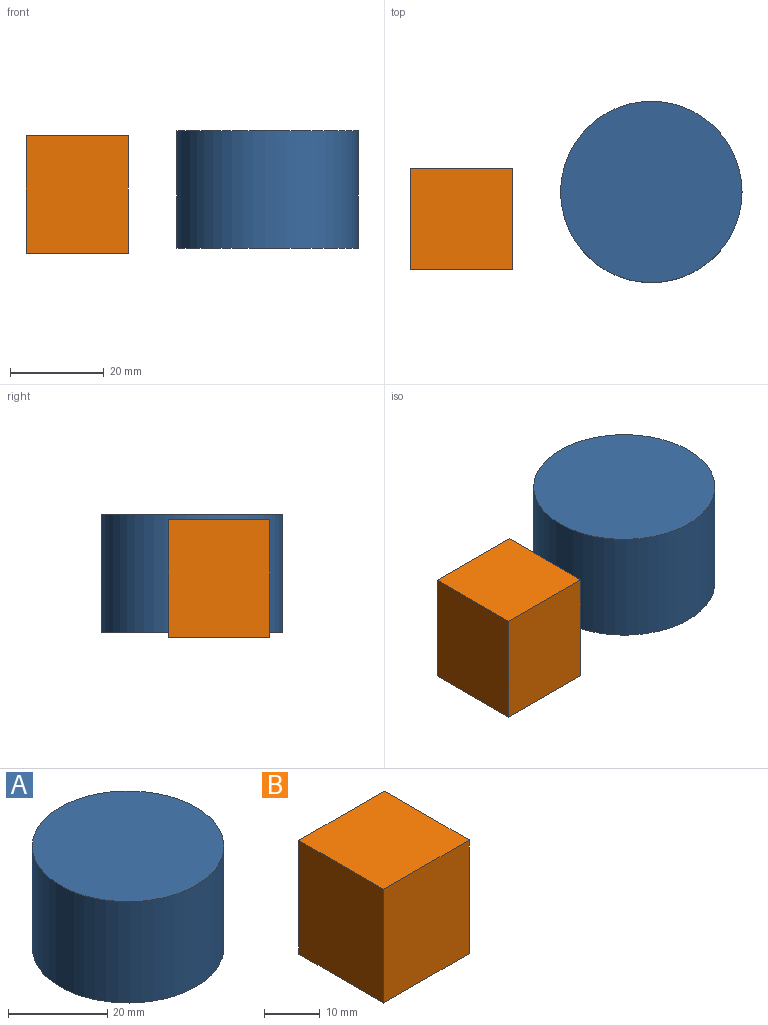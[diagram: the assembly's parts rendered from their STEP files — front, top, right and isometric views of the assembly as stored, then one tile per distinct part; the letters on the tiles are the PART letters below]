
ASSEMBLY  parts=2 mates=1
PART A: 3 faces, bbox 38.6x38.6x25 mm
  f0: cylinder r=19.31mm len=38.63mm, axis (0,0,-1), area 3033.7mm2, adj f1,f2
  f1: plane 38.63x38.63mm, normal (0,0,1), area 1171.8mm2, adj f0
  f2: plane 38.63x38.63mm, normal (0,0,-1), area 1171.8mm2, adj f0
PART B: 6 faces, bbox 21.7x21.5x25 mm
  f0: plane 25x21.74mm, normal (0,1,0), area 543.5mm2, adj f1,f3,f4,f5
  f1: plane 25x21.55mm, normal (-1,0,0), area 538.7mm2, adj f0,f2,f4,f5
  f2: plane 25x21.74mm, normal (0,-1,0), area 543.5mm2, adj f1,f3,f4,f5
  f3: plane 25x21.55mm, normal (1,0,0), area 538.7mm2, adj f0,f2,f4,f5
  f4: plane 21.74x21.55mm, normal (0,0,1), area 468.4mm2, adj f0,f1,f2,f3
  f5: plane 21.74x21.55mm, normal (0,0,-1), area 468.4mm2, adj f0,f1,f2,f3
PLACE A t=(60.85,24.6,4.92)mm
PLACE B t=(9.43,8.01,3.85)mm
MATE parallel A.f0 <-> B.f4  axis (0,0,1) through (60.85,24.6,29.92)mm
